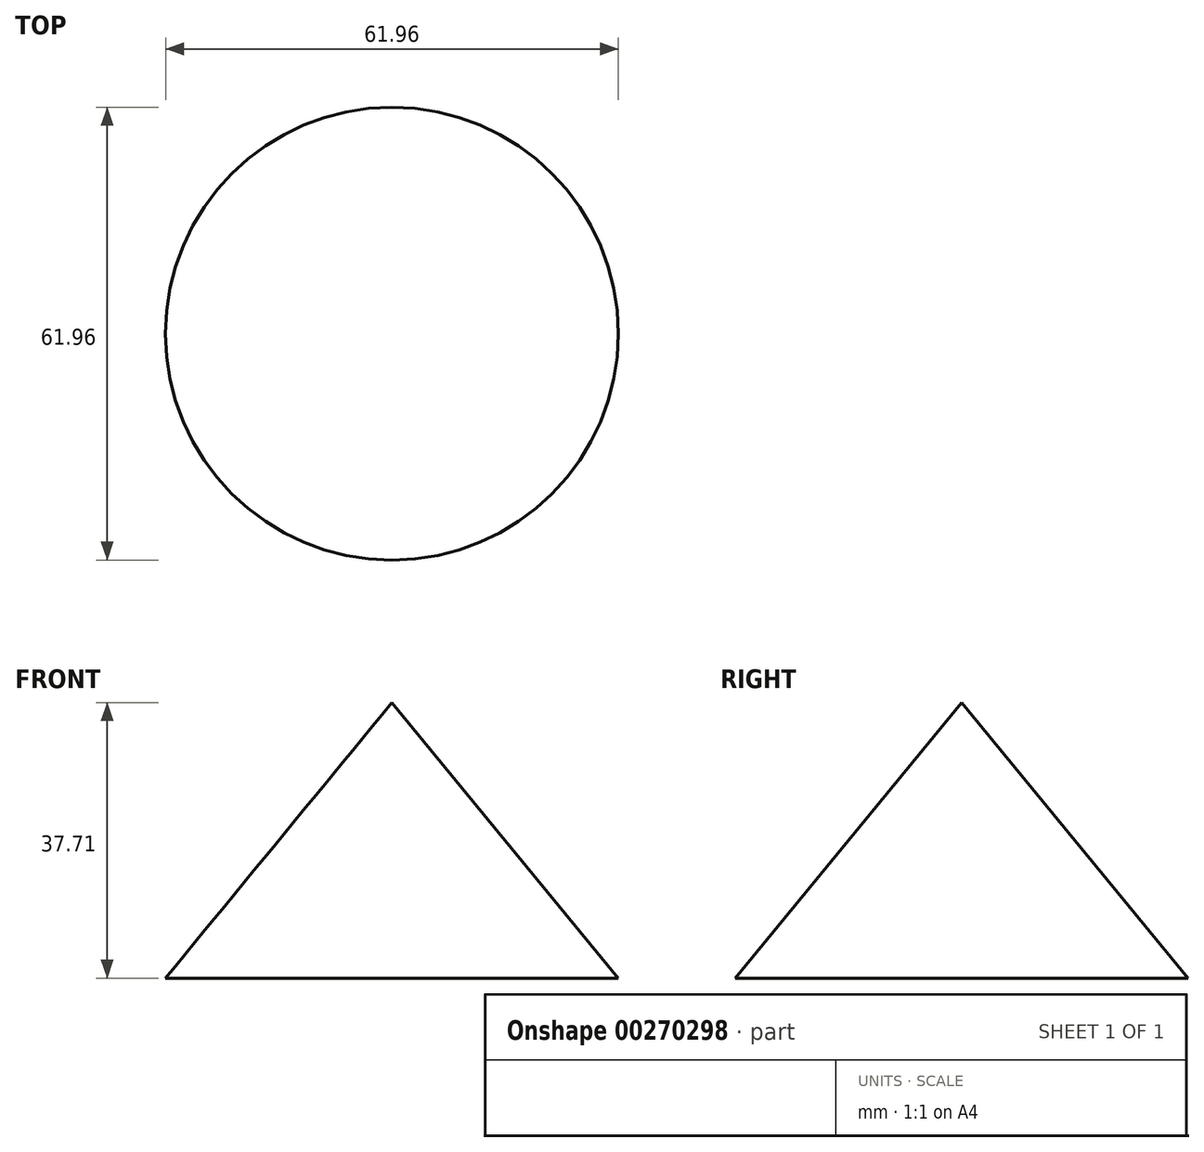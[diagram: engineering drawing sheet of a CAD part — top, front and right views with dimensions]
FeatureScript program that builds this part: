
annotation { "Feature Type Name" : "Feature", "Feature Type Description" : "" }
export const myFeature = defineFeature(function(context is Context, id is Id, definition is map)
    precondition{}
    {
        {
            var Q0;
            Q0=qCreatedBy(makeId("Front.planeOp"),FACE);
            var sketch = newSketch(context, id + "F0", { "sketchPlane" : qUnion([Q0])});
            skLineSegment(sketch, "E0", {"start": v(0, 37.7) * mm, "end": v(0, 0) * mm});
            skLineSegment(sketch, "E1", {"start": v(0, 0) * mm, "end": v(30.98, 0) * mm});
            skLineSegment(sketch, "E2", {"start": v(30.98, 0) * mm, "end": v(0, 37.7) * mm});
            skSolve(sketch);
        }
        {
            var Q0;
            Q0=makeQuery(id+"F0.imprint","IMPRINT",FACE,{"disambiguationData":[TD([[makeQuery(id+"F0.imprint","IMPRINT",EDGE,{"derivedFrom":sQuery(id+"F0.wireOp",EDGE,"E0")}),1.0]])]});
            var Q1;
            Q1=sQuery(id+"F0.wireOp",EDGE,"E0");
            revolve(context, id + "F1", {"entities" : qUnion([Q0]), "axis" : qUnion([Q1]), "revolveType" : RevolveType.FULL});
        }
    });
